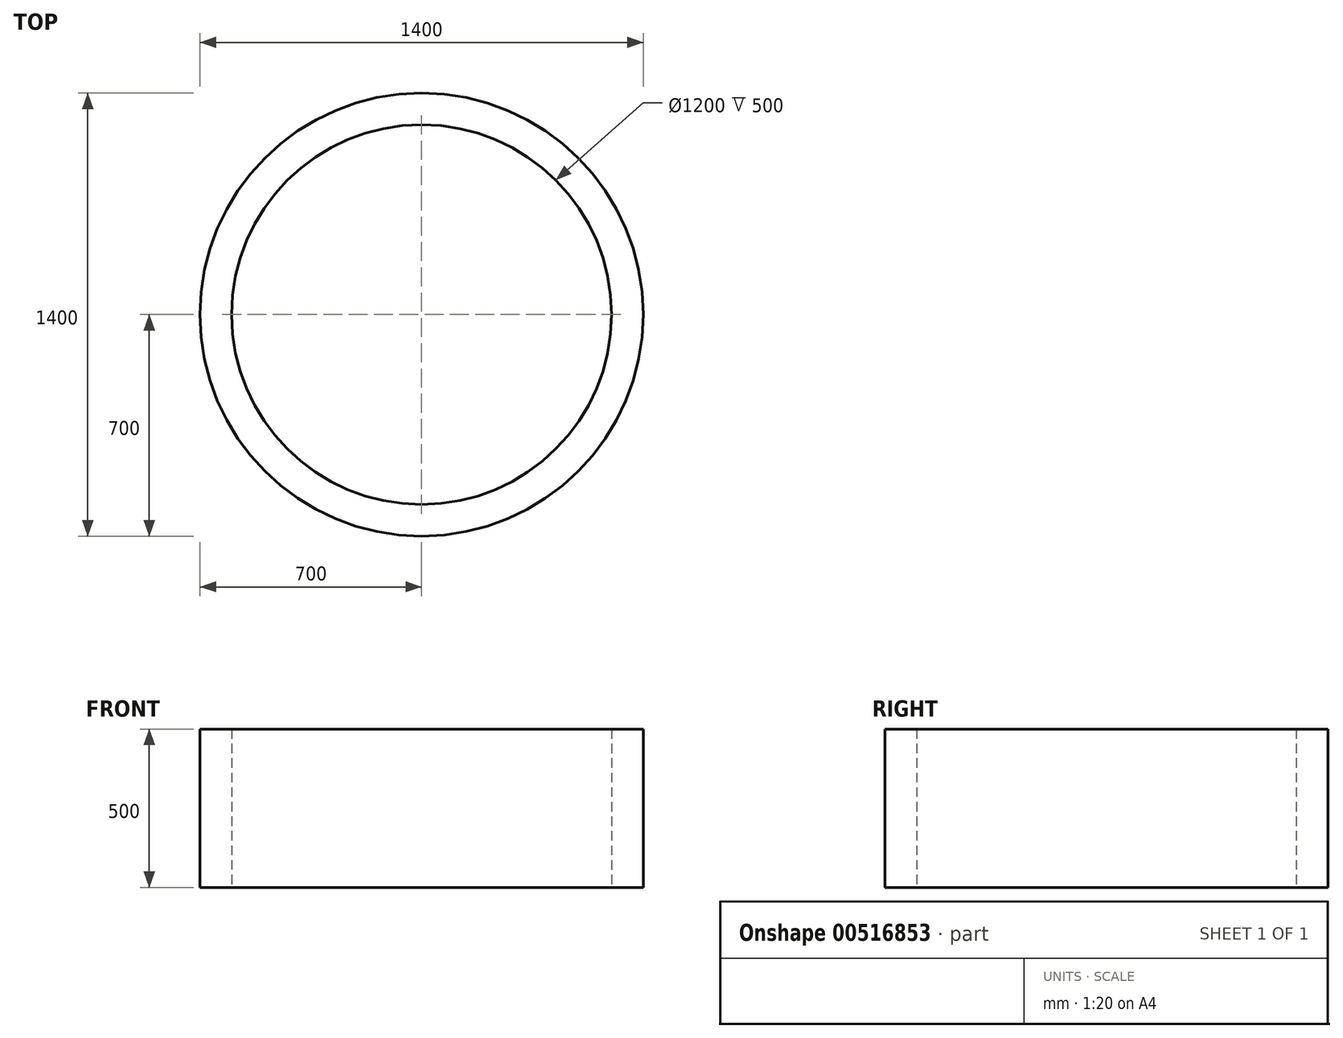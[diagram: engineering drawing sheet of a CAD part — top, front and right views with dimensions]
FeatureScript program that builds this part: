
annotation { "Feature Type Name" : "Feature", "Feature Type Description" : "" }
export const myFeature = defineFeature(function(context is Context, id is Id, definition is map)
    precondition{}
    {
        {
            var Q0;
            Q0=qCreatedBy(makeId("Top.planeOp"),FACE);
            var sketch = newSketch(context, id + "F0", { "sketchPlane" : qUnion([Q0])});
            skCircle(sketch, "E0", {"center": v(0, 0) * mm, "radius": 700 * mm});
            skCircle(sketch, "E1", {"center": v(0, 0) * mm, "radius": 600 * mm});
            skSolve(sketch);
        }
        {
            var Q0;
            Q0=makeQuery(id+"F0.imprint","IMPRINT",FACE,{"disambiguationData":[TD([[makeQuery(id+"F0.imprint","IMPRINT",EDGE,{"derivedFrom":sQuery(id+"F0.wireOp",EDGE,"E0")}),1.0]])]});
            extrude(context, id + "F1", {"entities" : qUnion([Q0]), "endBound" : BoundingType.SYMMETRIC, "depth" : 500 * mm});
        }
    });
